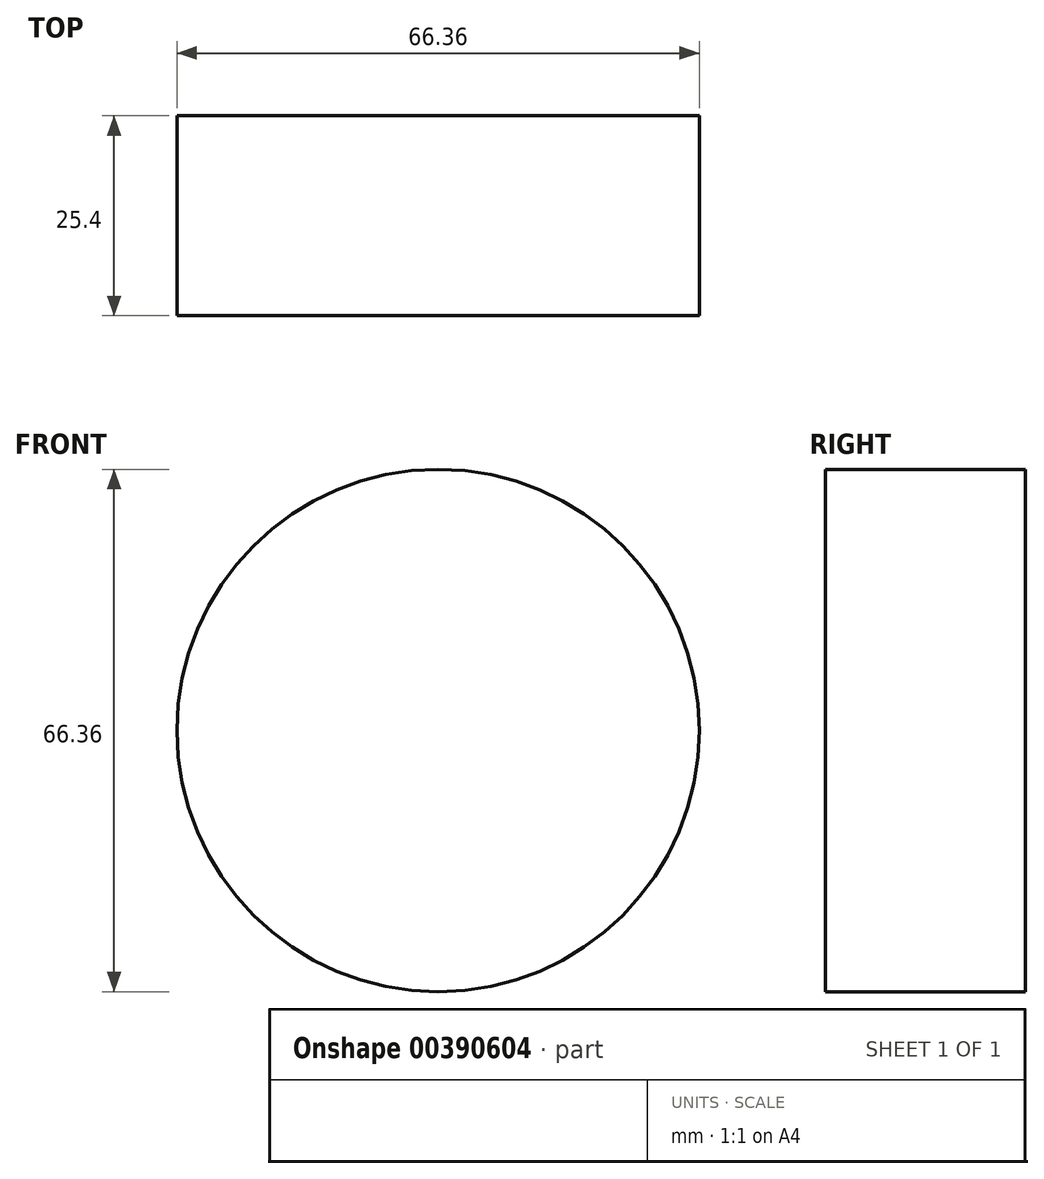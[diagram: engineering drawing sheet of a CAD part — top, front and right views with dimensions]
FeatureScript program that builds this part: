
annotation { "Feature Type Name" : "Feature", "Feature Type Description" : "" }
export const myFeature = defineFeature(function(context is Context, id is Id, definition is map)
    precondition{}
    {
        {
            var Q0;
            Q0=qCreatedBy(makeId("Front.planeOp"),FACE);
            var sketch = newSketch(context, id + "F0", { "sketchPlane" : qUnion([Q0])});
            skCircle(sketch, "E0", {"center": v(0, 0) * mm, "radius": 33.18 * mm});
            skSolve(sketch);
        }
        {
            var Q0;
            Q0=makeQuery(id+"F0.imprint","IMPRINT",FACE,{"disambiguationData":[TD([[makeQuery(id+"F0.imprint","IMPRINT",EDGE,{"derivedFrom":sQuery(id+"F0.wireOp",EDGE,"E0")}),1.0]])]});
            extrude(context, id + "F1", {"entities" : qUnion([Q0]), "depth" : 25.4 * mm, "offsetDistance" : 25.4 * mm});
        }
    });
